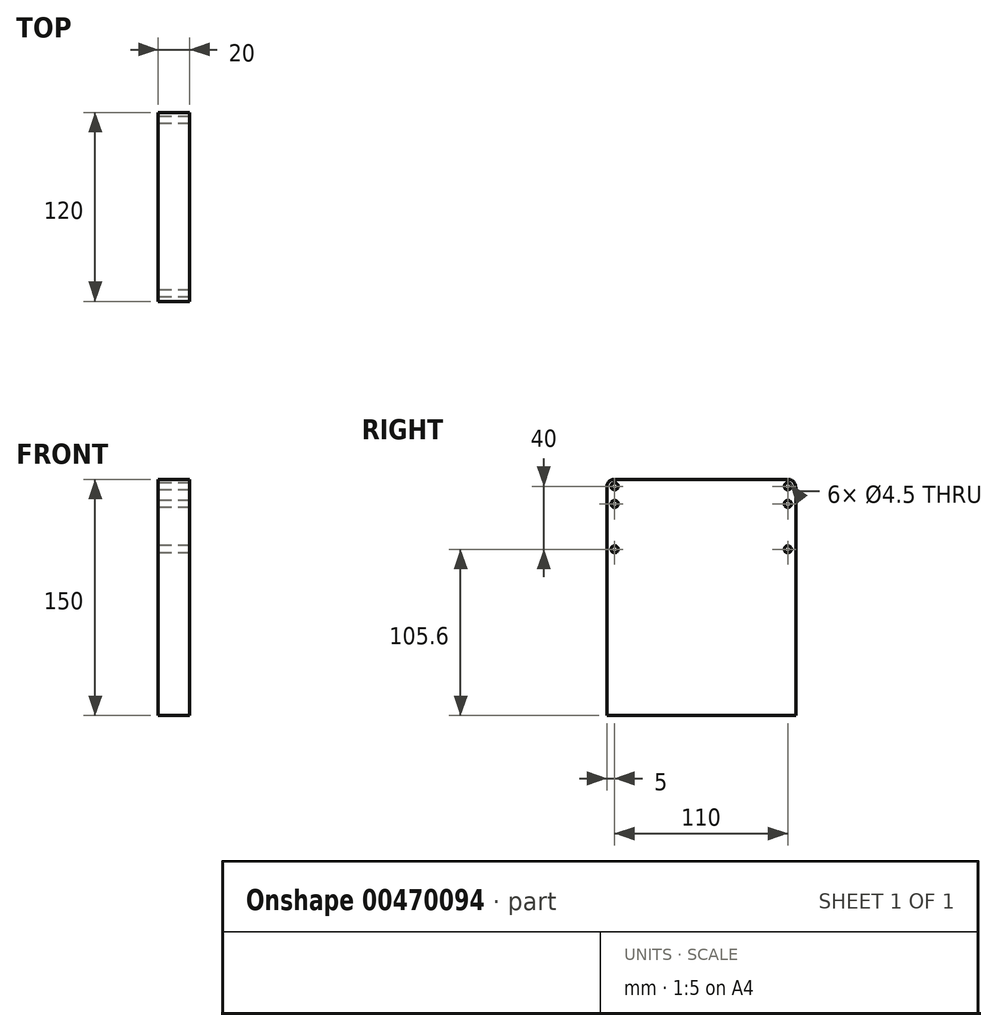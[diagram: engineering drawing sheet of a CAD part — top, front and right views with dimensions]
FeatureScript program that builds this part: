
annotation { "Feature Type Name" : "Feature", "Feature Type Description" : "" }
export const myFeature = defineFeature(function(context is Context, id is Id, definition is map)
    precondition{}
    {
        {
            var Q0;
            Q0=qCreatedBy(makeId("Right.planeOp"),FACE);
            var sketch = newSketch(context, id + "F0", { "sketchPlane" : qUnion([Q0])});
            skLineSegment(sketch, "E0.bottom", {"start": v(5, 150) * mm, "end": v(115, 150) * mm});
            skLineSegment(sketch, "E0.top", {"start": v(0, 0) * mm, "end": v(120, 0) * mm});
            skLineSegment(sketch, "E0.left", {"start": v(0, 145) * mm, "end": v(0, 0) * mm});
            skLineSegment(sketch, "E0.right", {"start": v(120, 145) * mm, "end": v(120, 0) * mm});
            skPoint(sketch, "E1.visualSharp", {"position": v(0, 150) * mm});
            skArc(sketch, "E1.filletArc", {"start": v(5, 150) * mm, "mid": v(1.46, 148.54) * mm, "end": v(0, 145) * mm});
            skPoint(sketch, "E2.visualSharp", {"position": v(120, 150) * mm});
            skArc(sketch, "E2.filletArc", {"start": v(120, 145) * mm, "mid": v(118.54, 148.54) * mm, "end": v(115, 150) * mm});
            skCircle(sketch, "E3", {"center": v(115, 145.6) * mm, "radius": 2.25 * mm});
            skCircle(sketch, "E4", {"center": v(5, 145.6) * mm, "radius": 2.25 * mm});
            skCircle(sketch, "E5", {"center": v(5, 134.4) * mm, "radius": 2.25 * mm});
            skCircle(sketch, "E6", {"center": v(115, 134.4) * mm, "radius": 2.25 * mm});
            skCircle(sketch, "E7", {"center": v(5, 105.6) * mm, "radius": 2.25 * mm});
            skLineSegment(sketch, "E8", {"start": v(60, 150) * mm, "end": v(60, 106.88) * mm, "construction": true});
            skCircle(sketch, "E9.MirrorC", {"center": v(115, 105.6) * mm, "radius": 2.25 * mm});
            skSolve(sketch);
        }
        {
            var Q0;
            Q0=makeQuery(id+"F0.imprint","IMPRINT",FACE,{"disambiguationData":[TD([[makeQuery(id+"F0.imprint","IMPRINT",EDGE,{"derivedFrom":sQuery(id+"F0.wireOp",EDGE,"E0.bottom")}),-1.0]])]});
            extrude(context, id + "F1", {"entities" : qUnion([Q0]), "depth" : 20 * mm});
        }
    });
